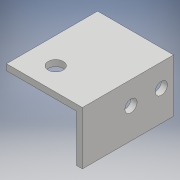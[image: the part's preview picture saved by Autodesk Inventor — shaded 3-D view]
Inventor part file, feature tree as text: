
AUTODESK INVENTOR PART (.ipt)
format: ipt  version: 2018 (Build 220112000, 112)  size: 115,712 bytes
history: native  units: mm
features: sketch x3, hole x2, other x1, extrude x1
ambient origin geometry x8: Origin, YZ Plane, XZ Plane, XY Plane, X Axis, Y Axis, Z Axis, Center Point
bodies: Body1 (feature_tree)
feature tree (7):
  other  "ソリッド1"
  extrude  "押し出し1"  Depth=35.0mm
  hole  "穴1"  [1 undecoded]
  hole  "穴2"  [1 undecoded]
  sketch  "スケッチ1"
  sketch  "スケッチ2"
  sketch  "スケッチ3"
note: 2 required parameter values undecoded (feature->parameter linkage not recoverable at this tier; creation-order binding heuristic only, values carry confidence <= 0.55)
